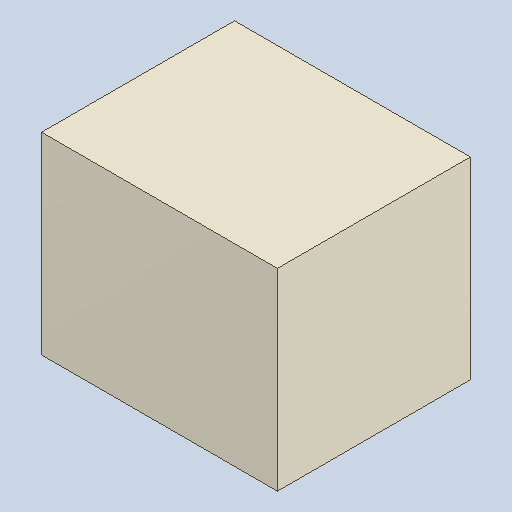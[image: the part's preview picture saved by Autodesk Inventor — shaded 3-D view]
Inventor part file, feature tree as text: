
AUTODESK INVENTOR PART (.ipt)
format: ipt  version: 2023.4 (Build 274418000, 418)  size: 81,920 bytes
history: native  units: mm
features: extrude x1
ambient origin geometry x8: Origin, YZ Plane, XZ Plane, XY Plane, X Axis, Y Axis, Z Axis, Center Point
bodies: Solid1 (feature_tree)
feature tree (1):
  extrude  "Extruded_1"  [1 undecoded]
note: 1 required parameter value undecoded (feature->parameter linkage not recoverable at this tier; creation-order binding heuristic only, values carry confidence <= 0.55)
